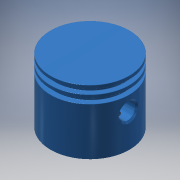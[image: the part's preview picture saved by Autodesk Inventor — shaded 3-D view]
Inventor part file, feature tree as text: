
AUTODESK INVENTOR PART (.ipt)
format: ipt  version: 2018 (Build 220112000, 112)  size: 297,472 bytes
history: native  units: mm
features: sketch x4, extrude x2, revolve x1, chamfer x1, hole x1, fillet x1
ambient origin geometry x8: Origin, YZ Plane, XZ Plane, XY Plane, X Axis, Y Axis, Z Axis, Center Point
bodies: Solid1 (feature_tree)
feature tree (10):
  revolve  "Revolution1"  [1 undecoded]
  extrude  "Extrusion1"  Depth=1.0mm
  extrude  "Extrusion2"  Depth=5.0mm
  chamfer  "Chamfer1"  Distance=0.1mm
  hole  "Hole1"  [1 undecoded]
  fillet  "Fillet1"  Radius=0.1mm
  sketch  "Sketch1"  dims[d0=12.0mm d3=1.0mm]
  sketch  "Sketch2"  dims[d4=1.5mm d5=1.0mm]
  sketch  "Sketch3"  dims[d6=1.5mm d7=5.0mm]
  sketch  "Sketch4"  dims[d8=1.0mm d9=0.1mm d10=19.5mm d11=0.1mm d12=90.0deg d13=10.0mm d14=5.0mm d15=11.0mm d16=0.0mm d17=5.0mm d18=10.0mm d19=36.75mm d20=0.0mm d21=0.5mm d22=2.0mm d23=45.0deg d24=8.0mm d25=8.0mm d26=2.013mm d27=5.0mm d28=4.0mm d29=2.0mm d30=90.0deg d31=7.6mm d32=0.0mm d33=1.0mm]
note: 2 required parameter values undecoded (feature->parameter linkage not recoverable at this tier; creation-order binding heuristic only, values carry confidence <= 0.55)